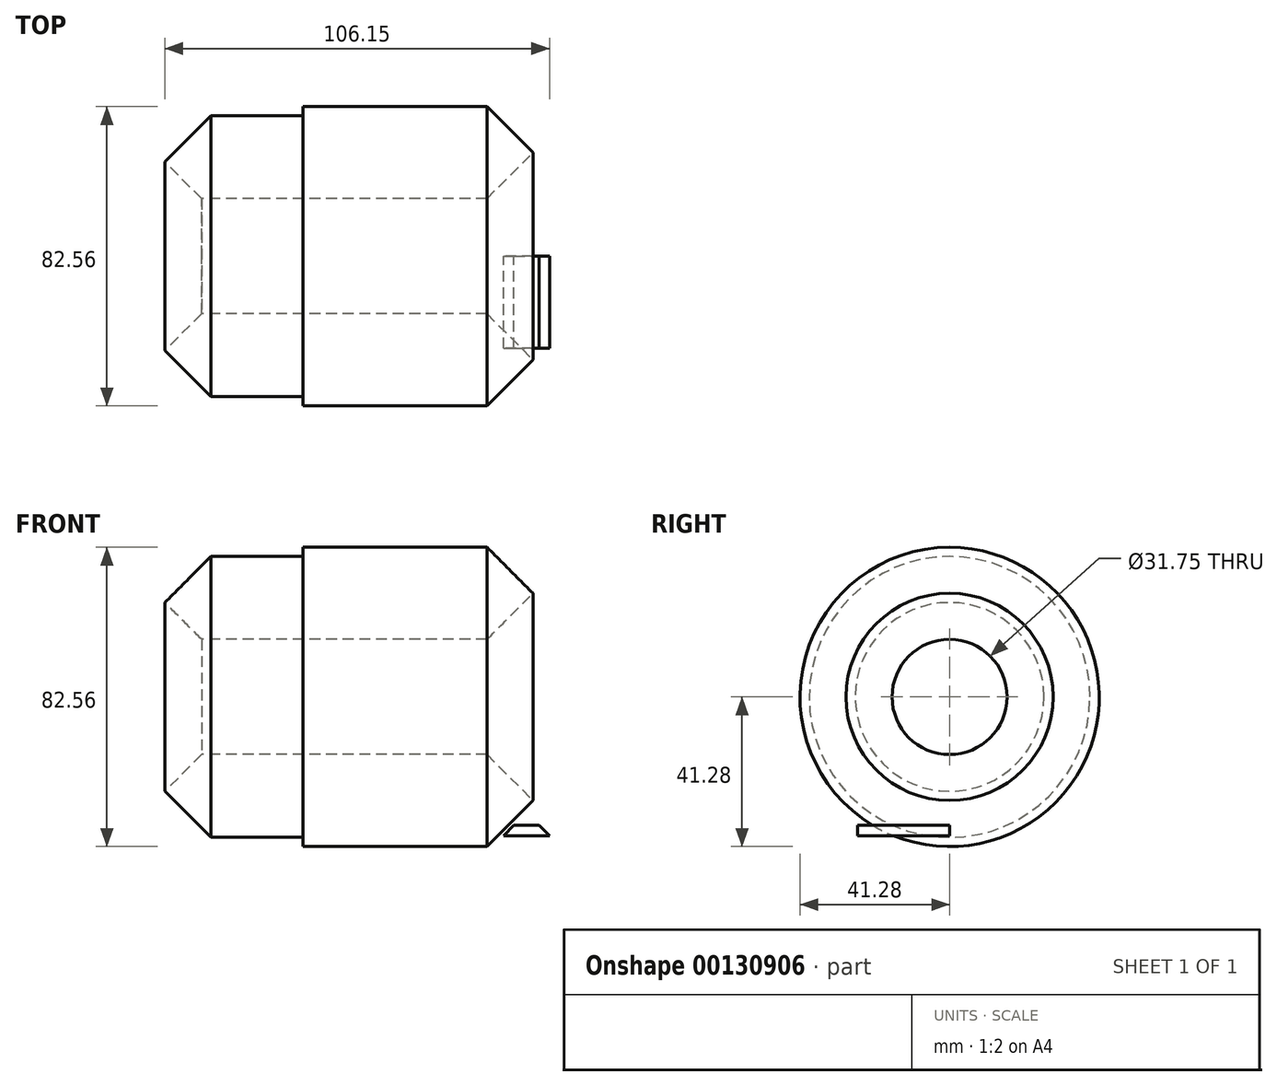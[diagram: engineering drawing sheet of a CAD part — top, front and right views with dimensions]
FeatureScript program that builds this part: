
annotation { "Feature Type Name" : "Feature", "Feature Type Description" : "" }
export const myFeature = defineFeature(function(context is Context, id is Id, definition is map)
    precondition{}
    {
        {
            var Q0;
            Q0=qCreatedBy(makeId("Front.planeOp"),FACE);
            var sketch = newSketch(context, id + "F0", { "sketchPlane" : qUnion([Q0])});
            skLineSegment(sketch, "E0", {"start": v(0, -26.04) * mm, "end": v(12.7, -38.74) * mm});
            skLineSegment(sketch, "E1", {"start": v(12.7, -38.74) * mm, "end": v(38.1, -38.74) * mm});
            skLineSegment(sketch, "E2", {"start": v(38.1, -38.74) * mm, "end": v(38.1, -41.28) * mm});
            skLineSegment(sketch, "E3", {"start": v(38.1, -41.28) * mm, "end": v(88.9, -41.28) * mm});
            skLineSegment(sketch, "E4", {"start": v(88.9, -41.28) * mm, "end": v(101.6, -28.57) * mm});
            skLineSegment(sketch, "E5", {"start": v(101.6, -28.57) * mm, "end": v(88.9, -15.87) * mm});
            skLineSegment(sketch, "E6", {"start": v(88.9, -15.87) * mm, "end": v(10.16, -15.88) * mm});
            skLineSegment(sketch, "E7", {"start": v(10.16, -15.88) * mm, "end": v(0, -26.04) * mm});
            skLineSegment(sketch, "E8", {"start": v(0, 0) * mm, "end": v(102.34, 0) * mm, "construction": true});
            skSolve(sketch);
        }
        {
            var Q0;
            Q0 = qSketchRegion(id + "F0", true);
            var Q1;
            Q1=sQuery(id+"F0.wireOp",EDGE,"E8");
            revolve(context, id + "F1", {"entities" : qUnion([Q0]), "axis" : qUnion([Q1]), "revolveType" : RevolveType.FULL});
        }
        {
            var Q0;
            Q0=qCreatedBy(makeId("Front.planeOp"),FACE);
            var sketch = newSketch(context, id + "F2", { "sketchPlane" : qUnion([Q0])});
            skLineSegment(sketch, "E9", {"start": v(93.45, -38.26) * mm, "end": v(96.35, -35.36) * mm});
            skLineSegment(sketch, "E10", {"start": v(96.35, -35.36) * mm, "end": v(103.25, -35.36) * mm});
            skLineSegment(sketch, "E11", {"start": v(103.25, -35.36) * mm, "end": v(106.15, -38.26) * mm});
            skLineSegment(sketch, "E12", {"start": v(106.15, -38.26) * mm, "end": v(93.45, -38.26) * mm});
            skSolve(sketch);
        }
        {
            var Q0;
            Q0 = qSketchRegion(id + "F2", true);
            extrude(context, id + "F3", {"entities" : qUnion([Q0]), "depth" : 25.4 * mm});
        }
    });
